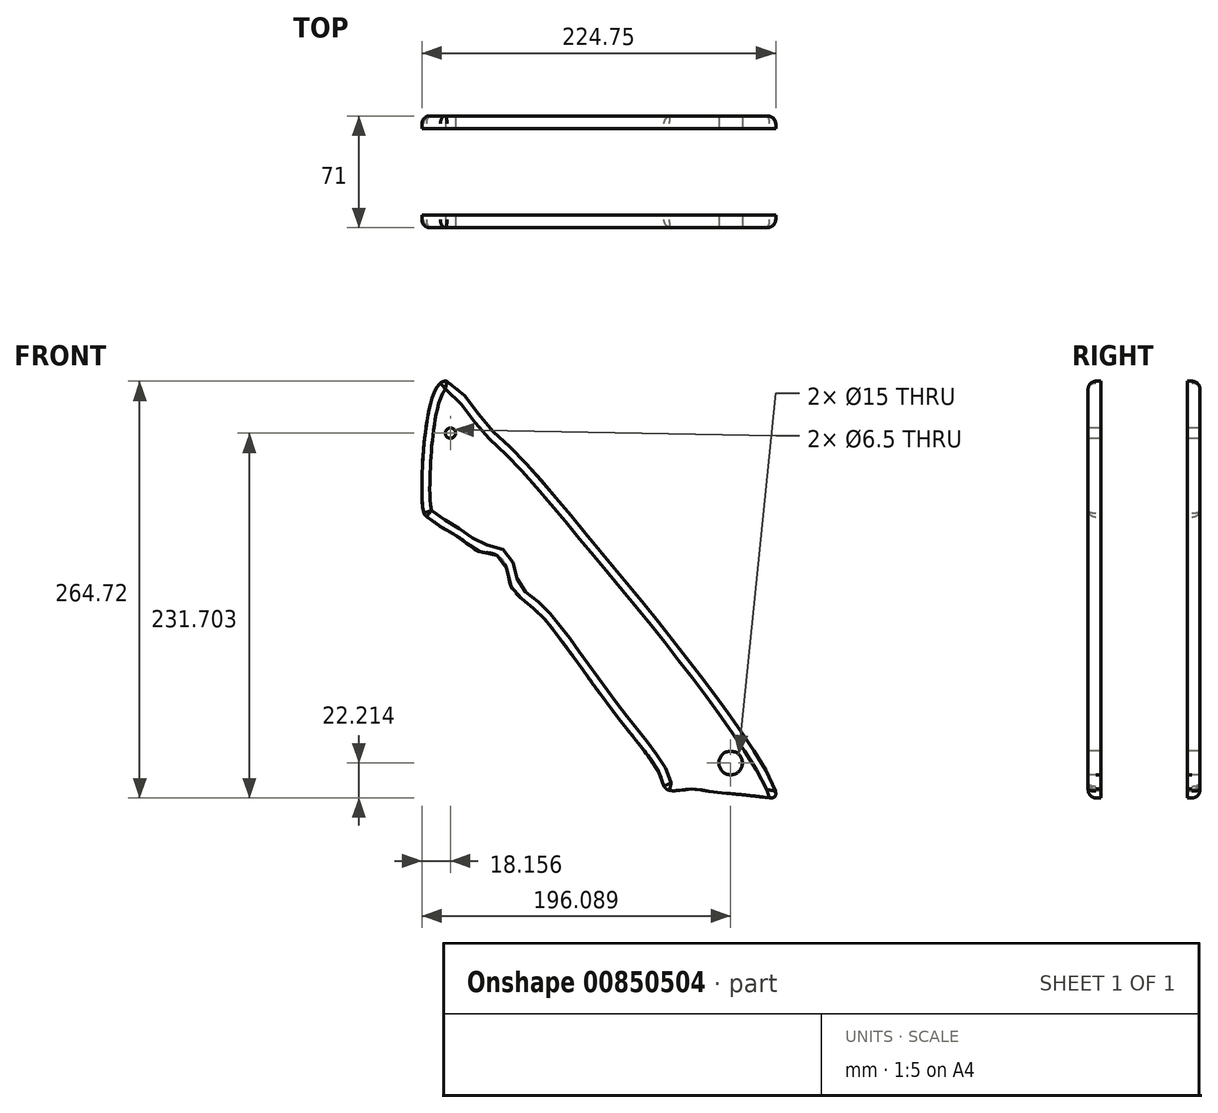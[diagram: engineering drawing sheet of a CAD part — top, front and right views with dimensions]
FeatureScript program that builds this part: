
annotation { "Feature Type Name" : "Feature", "Feature Type Description" : "" }
export const myFeature = defineFeature(function(context is Context, id is Id, definition is map)
    precondition{}
    {
        {
            var Q0;
            Q0=qCreatedBy(makeId("Front.planeOp"),FACE);
            var sketch = newSketch(context, id + "F0", { "sketchPlane" : qUnion([Q0])});
            skFitSpline(sketch, "E0", {"points": [v(-91.14, 126.54) * mm, v(-103.02, 46.9) * mm, v(-100.03, 40.75) * mm, v(-94.73, 37.1) * mm, v(-89.1, 33.13) * mm, v(-78.83, 27.16) * mm, v(-68.71, 19.56) * mm, v(-60.6, 18.1) * mm, v(-53.56, 15.07) * mm, v(-49.23, 6.4) * mm, v(-46.47, -4.24) * mm, v(-37.4, -13.3) * mm, v(-25.98, -23.55) * mm, v(20.11, -85.4) * mm, v(47.83, -123.28) * mm, v(52.33, -132.22) * mm, v(66.75, -131.95) * mm, v(78.33, -133.15) * mm, v(111.47, -136.8) * mm, v(121.08, -135.8) * mm, v(77, -64.76) * mm, v(8.32, 20.87) * mm, v(-45.36, 83.16) * mm, v(-64.32, 102.1) * mm, v(-91.14, 126.54) * mm]});
            skSolve(sketch);
        }
        {
            var Q0;
            Q0=makeQuery(id+"F0.imprint","IMPRINT",FACE,{"disambiguationData":[TD([[makeQuery(id+"F0.imprint","IMPRINT",EDGE,{"derivedFrom":sQuery(id+"F0.wireOp",EDGE,"E0")}),1.0]])]});
            extrude(context, id + "F1", {"entities" : qUnion([Q0]), "depth" : 8 * mm, "offsetDistance" : 25 * mm});
        }
        {
            var Q0;
            Q0=qCreatedBy(makeId("Front.planeOp"),FACE);
            cPlane(context, id + "F2", {"entities" : qUnion([Q0]), "cplaneType" : CPlaneType.OFFSET, "offset" : 35.5 * mm, "width" : 150 * mm, "height" : 150 * mm});
        }
        {
            var Q0;
            Q0=qCreatedBy(makeId("Right.planeOp"),FACE);
            var sketch = newSketch(context, id + "F3", { "sketchPlane" : qUnion([Q0])});
            skLineSegment(sketch, "E1.bottom", {"start": v(-15.53, -4.67) * mm, "end": v(-25.67, -4.67) * mm});
            skLineSegment(sketch, "E1.top", {"start": v(-15.53, -41.64) * mm, "end": v(-25.67, -41.64) * mm});
            skLineSegment(sketch, "E1.left", {"start": v(-15.53, -4.67) * mm, "end": v(-15.53, -41.64) * mm});
            skLineSegment(sketch, "E1.right", {"start": v(-25.67, -4.67) * mm, "end": v(-25.67, -41.64) * mm});
            skLineSegment(sketch, "E2.MirrorCS", {"start": v(-55.47, -4.67) * mm, "end": v(-55.47, -41.64) * mm});
            skLineSegment(sketch, "E3.MirrorCS", {"start": v(-55.47, -4.67) * mm, "end": v(-45.33, -4.67) * mm});
            skLineSegment(sketch, "E4.MirrorCS", {"start": v(-45.33, -4.67) * mm, "end": v(-45.33, -41.64) * mm});
            skLineSegment(sketch, "E5.MirrorCS", {"start": v(-55.47, -41.64) * mm, "end": v(-45.33, -41.64) * mm});
            skSolve(sketch);
        }
        {
            var Q0;
            Q0=makeQuery(id+"F1.opExtrude","SWEPT_BODY",BODY,{"disambiguationData":[OSD([sQuery(id+"F0.wireOp",EDGE,"E0")])]});
            var Q1;
            Q1=qCreatedBy(id+"F2.planeOp",FACE);
            mirror(context, id + "F4", {"entities" : qUnion([Q0]), "mirrorPlane" : qUnion([Q1])});
        }
        {
            var Q0;
            {var subQ0=sQuery(id+"F0.wireOp",EDGE,"E0");Q0=makeQuery(id+"F6.boolean.opBoolean","SPLIT",FACE,{"disambiguationData":[TD([makeQuery(id+"F6.opExtrude","SWEPT_FACE",FACE,{"disambiguationData":[OSD([sQuery(id+"F3.wireOp",EDGE,"E5.MirrorCS")])]})])],"derivedFrom":makeQuery(id+"F4.opPattern","COPY",FACE,{"derivedFrom":makeQuery(id+"F1.opExtrude","CAP_FACE",FACE,{"disambiguationData":[OSD([subQ0])],"isStart":true}),"instanceName":"1"})});}
            var sketch = newSketch(context, id + "F5", { "sketchPlane" : qUnion([Q0])});
            skCircle(sketch, "E6", {"center": v(92.52, -115.28) * mm, "radius": 7.5 * mm});
            skSolve(sketch);
        }
        {
            var Q0;
            Q0=makeQuery(id+"F3.imprint","IMPRINT",FACE,{"disambiguationData":[TD([[makeQuery(id+"F3.imprint","IMPRINT",EDGE,{"derivedFrom":sQuery(id+"F3.wireOp",EDGE,"E1.bottom")}),1.0]])]});
            var Q1;
            Q1=makeQuery(id+"F3.imprint","IMPRINT",FACE,{"disambiguationData":[TD([[makeQuery(id+"F3.imprint","IMPRINT",EDGE,{"derivedFrom":sQuery(id+"F3.wireOp",EDGE,"E2.MirrorCS")}),1.0]])]});
            extrude(context, id + "F6", {"entities" : qUnion([Q0, Q1]), "operationType" : NewBodyOperationType.REMOVE, "depth" : 500 * mm, "offsetDistance" : 25 * mm, "symmetric" : true});
        }
        {
            var Q0;
            Q0=makeQuery(id+"F5.imprint","IMPRINT",FACE,{"disambiguationData":[TD([[makeQuery(id+"F5.imprint","IMPRINT",EDGE,{"derivedFrom":sQuery(id+"F5.wireOp",EDGE,"E6")}),1.0]])]});
            extrude(context, id + "F7", {"entities" : qUnion([Q0]), "operationType" : NewBodyOperationType.REMOVE, "oppositeDirection" : true, "depth" : 10 * mm, "offsetDistance" : 25 * mm});
        }
        {
            var Q0;
            Q0=makeQuery(id+"F1.opExtrude","CAP_FACE",FACE,{"disambiguationData":[OSD([sQuery(id+"F0.wireOp",EDGE,"E0")])],"isStart":false});
            var sketch = newSketch(context, id + "F8", { "sketchPlane" : qUnion([Q0])});
            skCircle(sketch, "E7", {"center": v(92.52, -115.28) * mm, "radius": 7.5 * mm});
            skSolve(sketch);
        }
        {
            var Q0;
            Q0 = qSketchRegion(id + "F8", true);
            extrude(context, id + "F9", {"entities" : qUnion([Q0]), "operationType" : NewBodyOperationType.REMOVE, "oppositeDirection" : true, "depth" : 10 * mm, "offsetDistance" : 25 * mm});
        }
        {
            var Q0;
            {var subQ0=sQuery(id+"F0.wireOp",EDGE,"E0");Q0=makeQuery(id+"F6.boolean.opBoolean","SPLIT",FACE,{"disambiguationData":[TD([makeQuery(id+"F6.opExtrude","SWEPT_FACE",FACE,{"disambiguationData":[OSD([sQuery(id+"F3.wireOp",EDGE,"E3.MirrorCS")])]})])],"derivedFrom":makeQuery(id+"F4.opPattern","COPY",FACE,{"derivedFrom":makeQuery(id+"F1.opExtrude","CAP_FACE",FACE,{"disambiguationData":[OSD([subQ0])],"isStart":true}),"instanceName":"1"})});}
            var sketch = newSketch(context, id + "F10", { "sketchPlane" : qUnion([Q0])});
            skCircle(sketch, "E8", {"center": v(-85.41, 94.21) * mm, "radius": 3.25 * mm});
            skSolve(sketch);
        }
        {
            var Q0;
            Q0 = qSketchRegion(id + "F10", true);
            extrude(context, id + "F11", {"entities" : qUnion([Q0]), "operationType" : NewBodyOperationType.REMOVE, "oppositeDirection" : true, "depth" : 10 * mm, "offsetDistance" : 25 * mm});
        }
        {
            var Q0;
            Q0=makeQuery(id+"F1.opExtrude","CAP_FACE",FACE,{"disambiguationData":[OSD([sQuery(id+"F0.wireOp",EDGE,"E0")])],"isStart":false});
            var sketch = newSketch(context, id + "F12", { "sketchPlane" : qUnion([Q0])});
            skCircle(sketch, "E9", {"center": v(-85.41, 94.21) * mm, "radius": 3.25 * mm});
            skSolve(sketch);
        }
        {
            var Q0;
            Q0=makeQuery(id+"F12.imprint","IMPRINT",FACE,{"disambiguationData":[TD([[makeQuery(id+"F12.imprint","IMPRINT",EDGE,{"derivedFrom":sQuery(id+"F12.wireOp",EDGE,"E9")}),1.0]])]});
            extrude(context, id + "F13", {"entities" : qUnion([Q0]), "operationType" : NewBodyOperationType.REMOVE, "oppositeDirection" : true, "depth" : 10 * mm, "offsetDistance" : 25 * mm});
        }
        {
            var Q0;
            Q0=makeQuery(id+"F4.opPattern","COPY",FACE,{"derivedFrom":makeQuery(id+"F1.opExtrude","CAP_FACE",FACE,{"disambiguationData":[OSD([sQuery(id+"F0.wireOp",EDGE,"E0")])],"isStart":false}),"instanceName":"1"});
            var sketch = newSketch(context, id + "F14", { "sketchPlane" : qUnion([Q0])});
            skSolve(sketch);
        }
        {
            var Q0;
            Q0=makeQuery(id+"F4.opPattern","COPY",EDGE,{"derivedFrom":makeQuery(id+"F1.opExtrude","CAP_EDGE",EDGE,{"disambiguationData":[OSD([sQuery(id+"F0.wireOp",EDGE,"E0")])],"isStart":true}),"instanceName":"1"});
            var Q1;
            Q1=makeQuery(id+"F1.opExtrude","CAP_EDGE",EDGE,{"disambiguationData":[OSD([sQuery(id+"F0.wireOp",EDGE,"E0")])],"isStart":true});
            fillet(context, id + "F15", {"entities" : qUnion([Q0, Q1]), "radius" : 5 * mm, "tangentPropagation" : true, "allowEdgeOverflow" : false});
        }
    });
